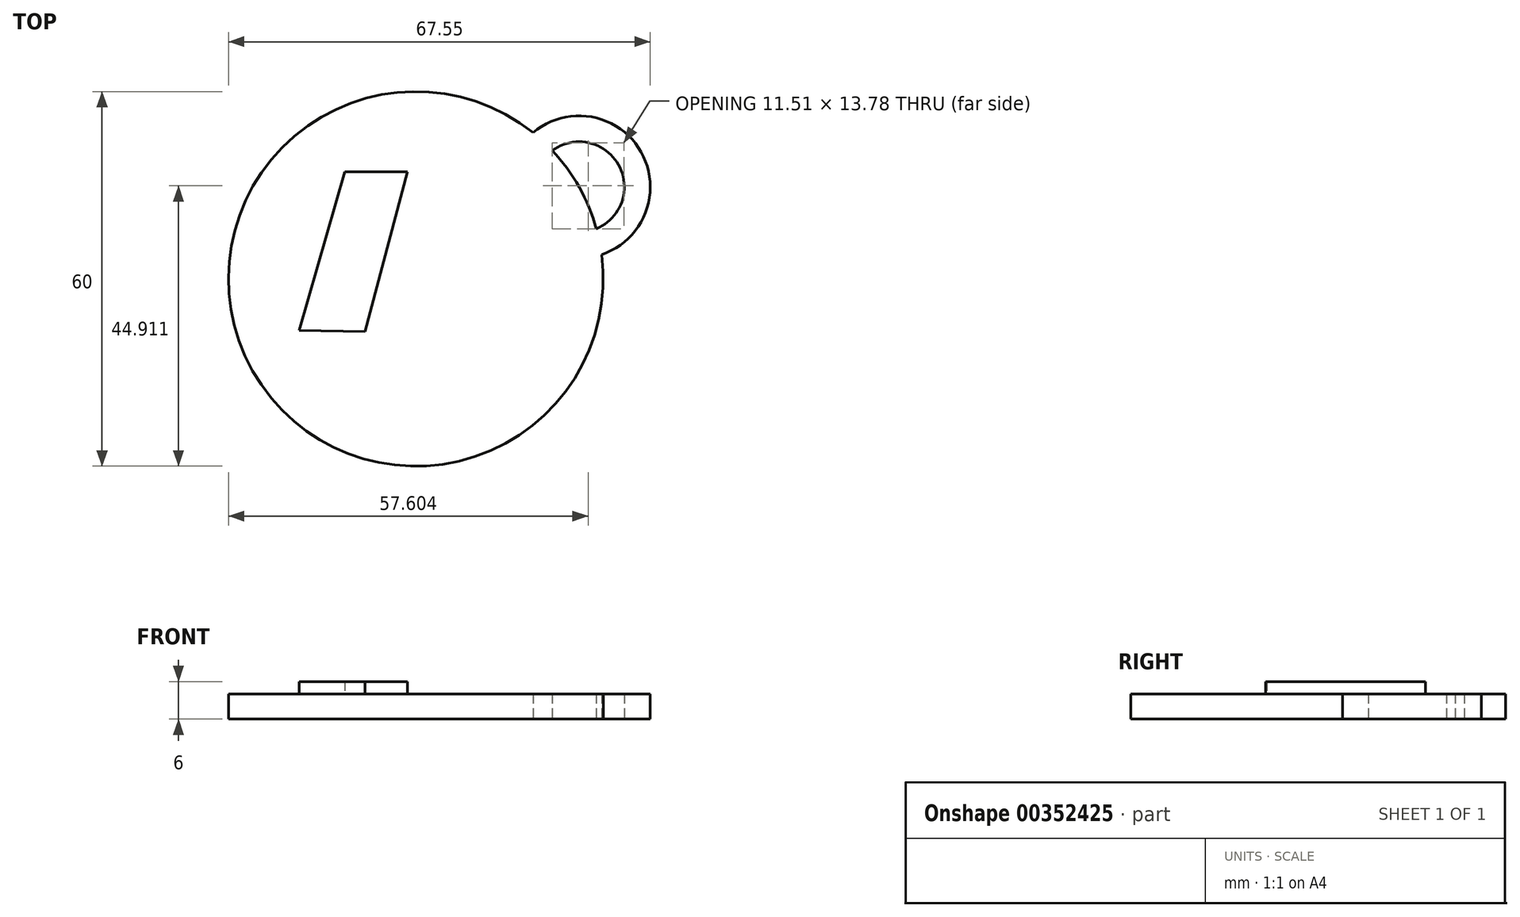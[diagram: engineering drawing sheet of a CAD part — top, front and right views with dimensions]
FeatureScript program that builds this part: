
annotation { "Feature Type Name" : "Feature", "Feature Type Description" : "" }
export const myFeature = defineFeature(function(context is Context, id is Id, definition is map)
    precondition{}
    {
        {
            var Q0;
            Q0=qCreatedBy(makeId("Top.planeOp"),FACE);
            var sketch = newSketch(context, id + "F0", { "sketchPlane" : qUnion([Q0])});
            skArc(sketch, "E0", {"start": v(29.09, 8.2) * mm, "mid": v(26.32, 14.9) * mm, "end": v(22.03, 20.74) * mm});
            skArc(sketch, "E1", {"start": v(29.93, 4.08) * mm, "mid": v(36.26, 20.5) * mm, "end": v(18.94, 23.6) * mm});
            skArc(sketch, "E2", {"start": v(29.09, 8.2) * mm, "mid": v(32.64, 18.45) * mm, "end": v(22.03, 20.74) * mm});
            skArc(sketch, "E3.trimOffspring", {"start": v(18.94, 23.6) * mm, "mid": v(-25.96, -14.54) * mm, "end": v(29.93, 4.08) * mm});
            skSolve(sketch);
        }
        {
            var Q0;
            Q0 = qSketchRegion(id + "F0", true);
            extrude(context, id + "F1", {"entities" : qUnion([Q0]), "depth" : 4 * mm});
        }
        {
            var Q0;
            Q0=makeQuery(id+"F1.opExtrude","CAP_FACE",FACE,{"disambiguationData":[OSD([sQuery(id+"F0.wireOp",EDGE,"E0"),sQuery(id+"F0.wireOp",EDGE,"E1"),sQuery(id+"F0.wireOp",EDGE,"E2"),sQuery(id+"F0.wireOp",EDGE,"E3.trimOffspring")])],"isStart":false});
            var sketch = newSketch(context, id + "F2", { "sketchPlane" : qUnion([Q0])});
            skLineSegment(sketch, "E4", {"start": v(-18.5, -8.07) * mm, "end": v(-11.19, 17.33) * mm});
            skLineSegment(sketch, "E5", {"start": v(-11.19, 17.33) * mm, "end": v(-1.15, 17.33) * mm});
            skLineSegment(sketch, "E6", {"start": v(-1.15, 17.33) * mm, "end": v(-7.96, -8.27) * mm});
            skLineSegment(sketch, "E7", {"start": v(-7.96, -8.27) * mm, "end": v(-18.5, -8.07) * mm});
            skLineSegment(sketch, "E8", {"start": v(-1.15, -8.27) * mm, "end": v(4.8, 17.33) * mm});
            skLineSegment(sketch, "E9", {"start": v(4.8, 17.33) * mm, "end": v(15.21, 17.33) * mm});
            skLineSegment(sketch, "E10", {"start": v(15.21, 17.54) * mm, "end": v(10.26, -8.07) * mm});
            skLineSegment(sketch, "E11", {"start": v(10.26, -7.89) * mm, "end": v(-1.15, -8.27) * mm});
            skSolve(sketch);
        }
        {
            var Q0;
            Q0 = qSketchRegion(id + "F2", true);
            extrude(context, id + "F3", {"entities" : qUnion([Q0]), "operationType" : NewBodyOperationType.ADD, "depth" : 2 * mm});
        }
    });
